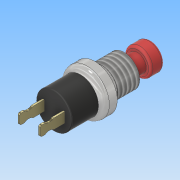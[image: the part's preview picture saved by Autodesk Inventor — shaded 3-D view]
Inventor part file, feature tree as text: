
AUTODESK INVENTOR PART (.ipt)
format: ipt  version: 2019 (Build 230136000, 136)  size: 215,552 bytes
history: native  units: mm
features: sketch x8, extrude x7, fillet x2, revolve x1, thread x1
ambient origin geometry x8: Origin, YZ Plane, XZ Plane, XY Plane, X Axis, Y Axis, Z Axis, Center Point
bodies: Solid1 (feature_tree)
feature tree (19):
  extrude  "Extrusion1"  Depth=6.0mm TaperAngle=0.0deg
  extrude  "Extrusion2"  Depth=2.25mm
  extrude  "Extrusion3"  Depth=2.5mm
  revolve  "Revolution1"  [1 undecoded]
  extrude  "Extrusion4"  Depth=2.0mm
  extrude  "Extrusion6"  Depth=5.5mm TaperAngle=0.0deg
  thread  "Thread1"  [1 undecoded]
  extrude  "Extrusion7"  Depth=5.0mm
  extrude  "Extrusion8"  Depth=0.2mm
  fillet  "Fillet1"  Radius=1.5mm
  fillet  "Fillet2"  Radius=7.05mm
  sketch  "Sketch1"  dims[d0=8.0mm d1=6.0mm d2=0.0mm]
  sketch  "Sketch2"  dims[d3=2.25mm d6=2.25mm d9=0.4mm]
  sketch  "Sketch3"  dims[d10=0.4mm d11=2.5mm]
  sketch  "Sketch4"  dims[d12=2.5mm d13=5.5mm d14=0.0mm]
  sketch  "Sketch5"  dims[d15=2.5mm d16=2.0mm]
  sketch  "Sketch7"  dims[d17=45.0deg d18=5.5mm d19=0.0mm d20=3.2mm]
  sketch  "Sketch8"  dims[d21=5.0mm d22=1.8mm]
  sketch  "Sketch9"  dims[d23=90.0deg d24=7.0mm d25=1.5mm d26=0.0mm d29=7.05mm d30=5.0mm d31=0.0mm d32=10.0mm d33=0.0mm d34=4.0mm d35=3.0mm d36=0.0mm d37=6.0mm d38=3.0mm d39=0.0mm d40=0.5mm d41=0.2mm]
note: 2 required parameter values undecoded (feature->parameter linkage not recoverable at this tier; creation-order binding heuristic only, values carry confidence <= 0.55)